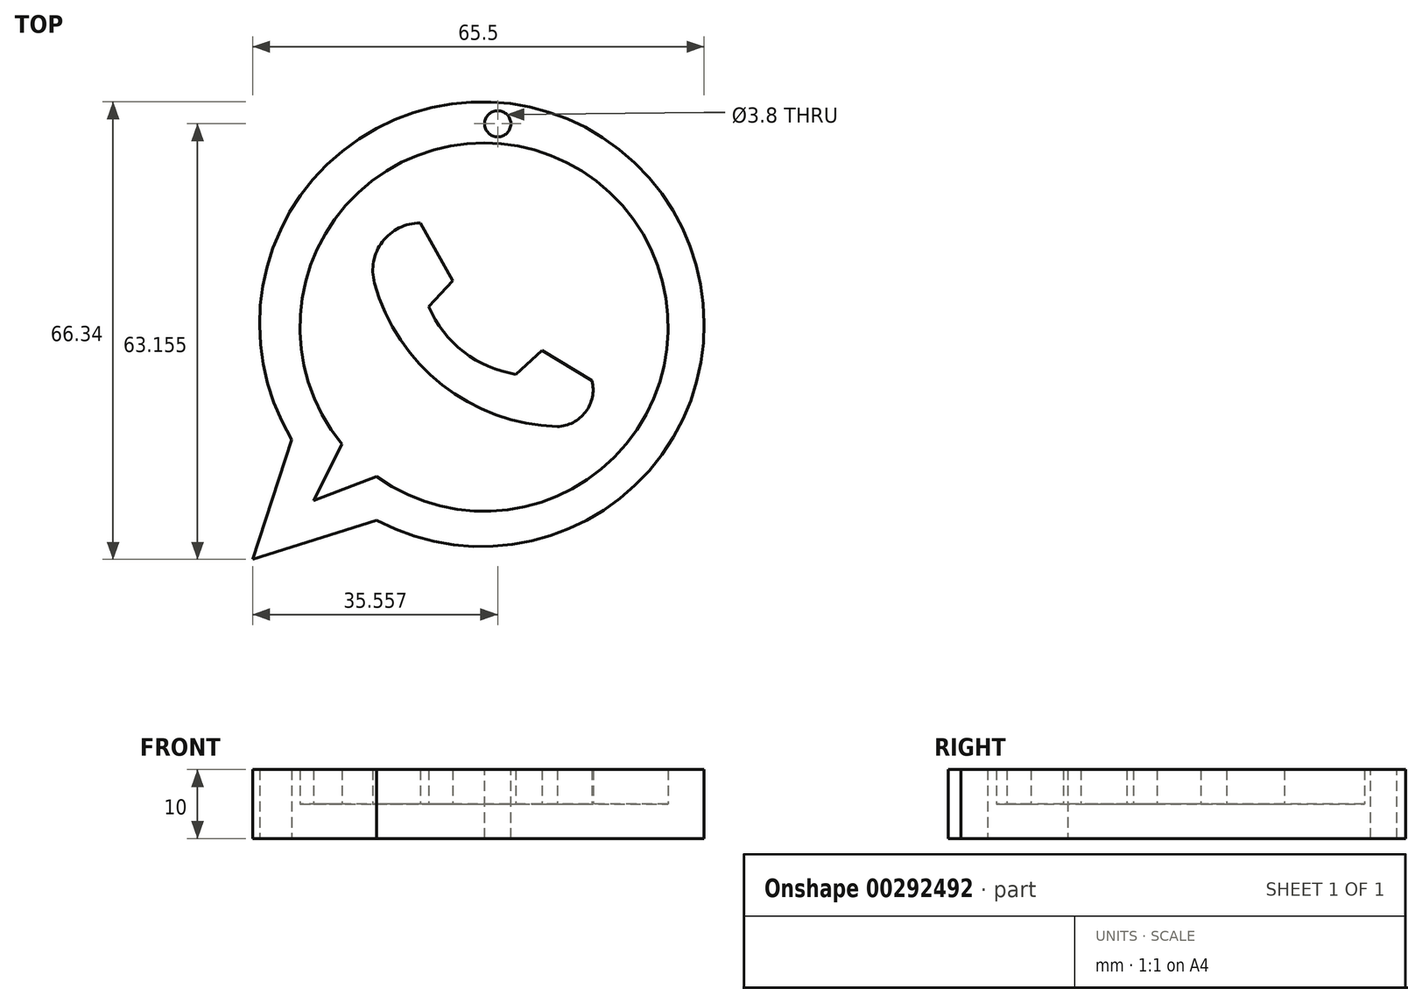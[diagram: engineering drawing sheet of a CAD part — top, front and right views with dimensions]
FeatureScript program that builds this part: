
annotation { "Feature Type Name" : "Feature", "Feature Type Description" : "" }
export const myFeature = defineFeature(function(context is Context, id is Id, definition is map)
    precondition{}
    {
        {
            var Q0;
            Q0=qCreatedBy(makeId("Top.planeOp"),FACE);
            var sketch = newSketch(context, id + "F0", { "sketchPlane" : qUnion([Q0])});
            skArc(sketch, "E0", {"start": v(5.05, -43.08) * mm, "mid": v(42.51, 8.73) * mm, "end": v(-7.26, -31.4) * mm});
            skLineSegment(sketch, "E1", {"start": v(-7.26, -31.4) * mm, "end": v(-12.94, -48.76) * mm});
            skLineSegment(sketch, "E2", {"start": v(5.05, -43.08) * mm, "end": v(-12.94, -48.76) * mm});
            skLineSegment(sketch, "E3", {"start": v(5.05, -36.77) * mm, "end": v(-4.1, -40.24) * mm});
            skLineSegment(sketch, "E4", {"start": v(-4.1, -40.24) * mm, "end": v(0, -32.04) * mm});
            skArc(sketch, "E5", {"start": v(5.05, -36.77) * mm, "mid": v(38.9, 4.4) * mm, "end": v(0, -32.04) * mm});
            skArc(sketch, "E6", {"start": v(4.73, -8.68) * mm, "mid": v(14.56, -23.46) * mm, "end": v(31.25, -29.51) * mm});
            skArc(sketch, "E7", {"start": v(11.36, 0) * mm, "mid": v(5.9, -2.7) * mm, "end": v(4.73, -8.68) * mm});
            skArc(sketch, "E8", {"start": v(31.25, -29.51) * mm, "mid": v(35.35, -27.4) * mm, "end": v(36.3, -22.88) * mm});
            skArc(sketch, "E9", {"start": v(12.62, -12.15) * mm, "mid": v(17.67, -18.68) * mm, "end": v(25.25, -21.94) * mm});
            skLineSegment(sketch, "E10", {"start": v(11.36, 0) * mm, "end": v(16.1, -8.36) * mm});
            skLineSegment(sketch, "E11", {"start": v(16.1, -8.36) * mm, "end": v(12.62, -12.15) * mm});
            skLineSegment(sketch, "E12", {"start": v(36.3, -22.88) * mm, "end": v(29.04, -18.46) * mm});
            skLineSegment(sketch, "E13", {"start": v(29.04, -18.46) * mm, "end": v(25.25, -21.94) * mm});
            skSolve(sketch);
        }
        {
            var Q0;
            Q0 = qSketchRegion(id + "F0", true);
            var Q1;
            Q1=makeQuery(id+"F0.imprint","IMPRINT",FACE,{"disambiguationData":[TD([[makeQuery(id+"F0.imprint","IMPRINT",EDGE,{"derivedFrom":sQuery(id+"F0.wireOp",EDGE,"E3")}),-1.0]])]});
            var Q2;
            Q2=makeQuery(id+"F0.imprint","IMPRINT",FACE,{"disambiguationData":[TD([[makeQuery(id+"F0.imprint","IMPRINT",EDGE,{"derivedFrom":sQuery(id+"F0.wireOp",EDGE,"E6")}),1.0]])]});
            extrude(context, id + "F1", {"entities" : qUnion([Q0, Q1, Q2]), "depth" : 5 * mm});
        }
        {
            var Q0;
            Q0=makeQuery(id+"F0.imprint","IMPRINT",FACE,{"disambiguationData":[TD([[makeQuery(id+"F0.imprint","IMPRINT",EDGE,{"derivedFrom":sQuery(id+"F0.wireOp",EDGE,"E6")}),1.0]])]});
            var Q1;
            Q1=makeQuery(id+"F0.imprint","IMPRINT",FACE,{"disambiguationData":[TD([[makeQuery(id+"F0.imprint","IMPRINT",EDGE,{"derivedFrom":sQuery(id+"F0.wireOp",EDGE,"E0")}),1.0]])]});
            extrude(context, id + "F2", {"entities" : qUnion([Q0, Q1]), "operationType" : NewBodyOperationType.ADD, "depth" : 10 * mm});
        }
        {
            var Q0;
            Q0=makeQuery(id+"F2.opExtrude","CAP_FACE",FACE,{"disambiguationData":[OSD([sQuery(id+"F0.wireOp",EDGE,"E0"),sQuery(id+"F0.wireOp",EDGE,"E1"),sQuery(id+"F0.wireOp",EDGE,"E2"),sQuery(id+"F0.wireOp",EDGE,"E3"),sQuery(id+"F0.wireOp",EDGE,"E4"),sQuery(id+"F0.wireOp",EDGE,"E5")])],"isStart":false});
            var sketch = newSketch(context, id + "F3", { "sketchPlane" : qUnion([Q0])});
            skCircle(sketch, "E14", {"center": v(22.62, 14.4) * mm, "radius": 1.9 * mm});
            skSolve(sketch);
        }
        {
            var Q0;
            Q0 = qSketchRegion(id + "F3", true);
            extrude(context, id + "F4", {"entities" : qUnion([Q0]), "operationType" : NewBodyOperationType.REMOVE, "oppositeDirection" : true, "depth" : 25 * mm});
        }
    });
